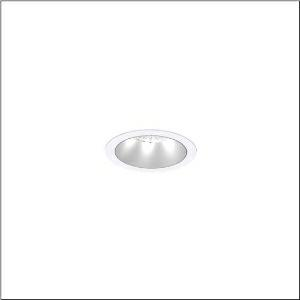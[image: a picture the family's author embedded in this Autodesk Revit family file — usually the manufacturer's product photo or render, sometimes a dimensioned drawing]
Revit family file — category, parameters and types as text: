
# Revit family: lunis_21_m_51db19ec91c
name_source: partatom
category: Lighting Fixtures
units: mm (PartAtom-declared; Revit-internal decimal feet)

## family parameters
Cut with Voids When Loaded = No
Host = Face
Light Source = No
Part Type = Normal
Room Calculation Point = No
Round Connector Dimension = Use Diameter
Shared = No

## types (1)
- --- (1 x LED, 3720 lm, 25.5 W, 6500K)
    Apparent Load = 26 VA
    CIE Flux Codes = 93 99 100 100 100
    Color Rendering = 80
    Color Temperature = 6500K
    Default Elevation = 1800 mm
    Description = Lunis 21,  M, downlight, light control with lens, of PMMA, anti glare with reflector, of PC, matt, light emission: direct distribution, LED rated luminous flux: 1.730lm, light colour: 830/840/865, with terminal, 5-pole, mains connection: 220..240V, AC/DC, 0/50..60Hz, housing, round, of diecast aluminium, traffic white (RAL 9016), diameter: 115mm, clamping range: 1..40mm, protection rating (complete): IP20, protection rating (on room side): IP54, insulation class (complete): insulation class II (safety insulation), certification: CE, impact resistance: IK03, packaging unit: 1 piece
    Height = 0 mm  [stored 0 ft]
    Lamp = 1 x LED
    Lamp Light Flux = 3720 lm
    Lamp Power = 25.5 W
    Lamp count = 1
    Length = 115 mm
    Luminous efficacy = 146 lm/W
    Manufacturer = Siteco
    ModVariant = No
    Model = 51DB19EC91C
    Mounting Place = Ceiling
    Mounting Type = Recessed
    Number of Poles = 1
    OnlyDefault = Yes
    Power Factor = 1
    Product Name = Lunis 21 M
    Product group = downlight
    ProductGroupID = 401
    Protection Class = Protection class II
    Protection Degree = IP 20
    RLX_Detail_Level = 1
    RLX_Emergency_Light_Flux = 0 lm
    RLX_Emergency_Type = 0
    RLX_Emergency_Type_DB = No
    RlxData = <blob elided: 14961 chars, md5=5e6ee565>
    Socket = socket
    Standby Power = 0 W
    System Light Flux = 3720 lm
    System Power = 26 W
    Type Comments = individual setting: colour temperature 6500K, luminous flux: 100 % | (ON | ON | OFF | OFF) | 700 mA
    Type Image = l_1290856.jpg
    URL = http://relux.com
    VarID = @adj_039021
    Voltage = 0 V
    Weight = 0.00 kg
    Width = 0 mm  [stored 0 ft]

note: [stored X ft] marks values corroborated as IEEE doubles in the binary element streams (Revit-internal decimal feet)

## geometry (parser evidence)
native form markers: Sweep x10
no freeform markers — native parametric forms only
